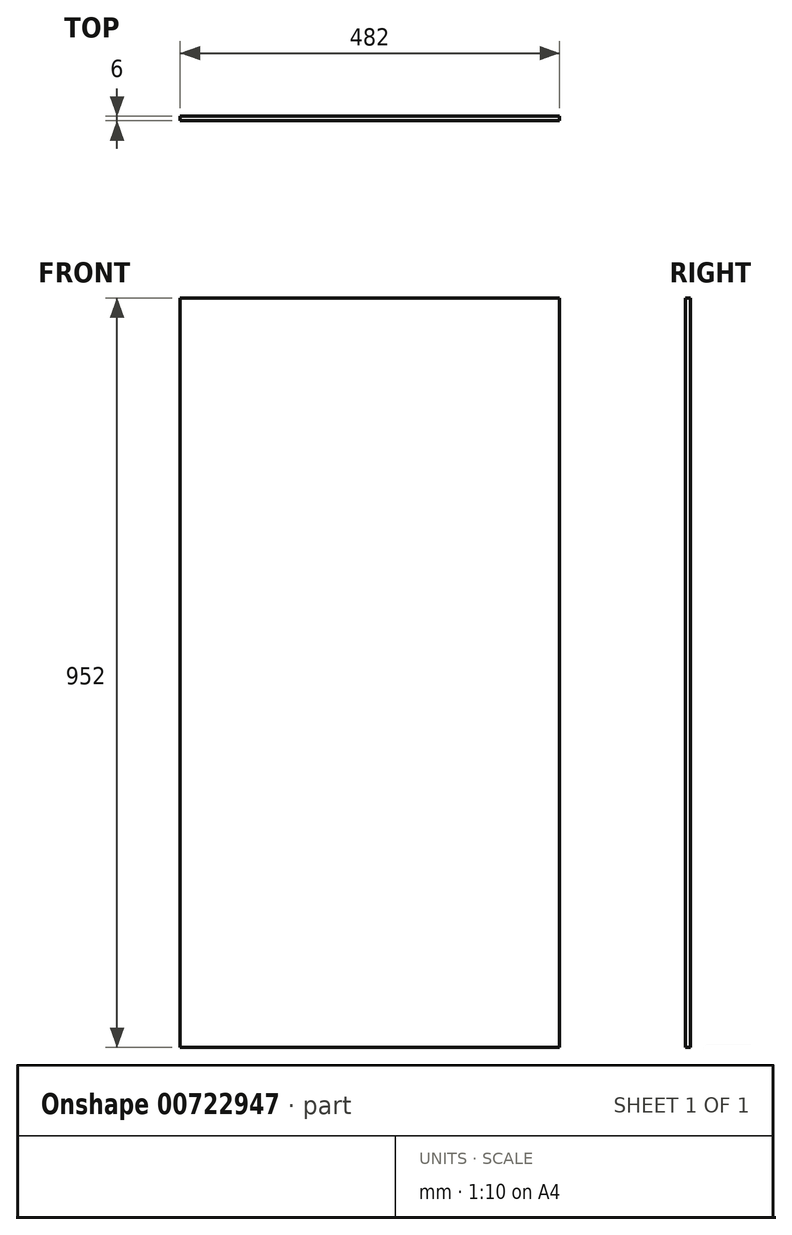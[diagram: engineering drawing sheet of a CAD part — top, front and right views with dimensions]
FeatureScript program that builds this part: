
annotation { "Feature Type Name" : "Feature", "Feature Type Description" : "" }
export const myFeature = defineFeature(function(context is Context, id is Id, definition is map)
    precondition{}
    {
        {
            var Q0;
            Q0=qCreatedBy(makeId("Front.planeOp"),FACE);
            var sketch = newSketch(context, id + "F0", { "sketchPlane" : qUnion([Q0])});
            skLineSegment(sketch, "E0.bottom", {"start": v(-350.74, 451.04) * mm, "end": v(131.26, 451.04) * mm});
            skLineSegment(sketch, "E0.top", {"start": v(-350.74, -500.96) * mm, "end": v(131.26, -500.96) * mm});
            skLineSegment(sketch, "E0.left", {"start": v(-350.74, 451.04) * mm, "end": v(-350.74, -500.96) * mm});
            skLineSegment(sketch, "E0.right", {"start": v(131.26, 451.04) * mm, "end": v(131.26, -500.96) * mm});
            skSolve(sketch);
        }
        {
            var Q0;
            Q0 = qSketchRegion(id + "F0", true);
            extrude(context, id + "F1", {"entities" : qUnion([Q0]), "depth" : 6 * mm, "offsetDistance" : 25 * mm});
        }
    });
